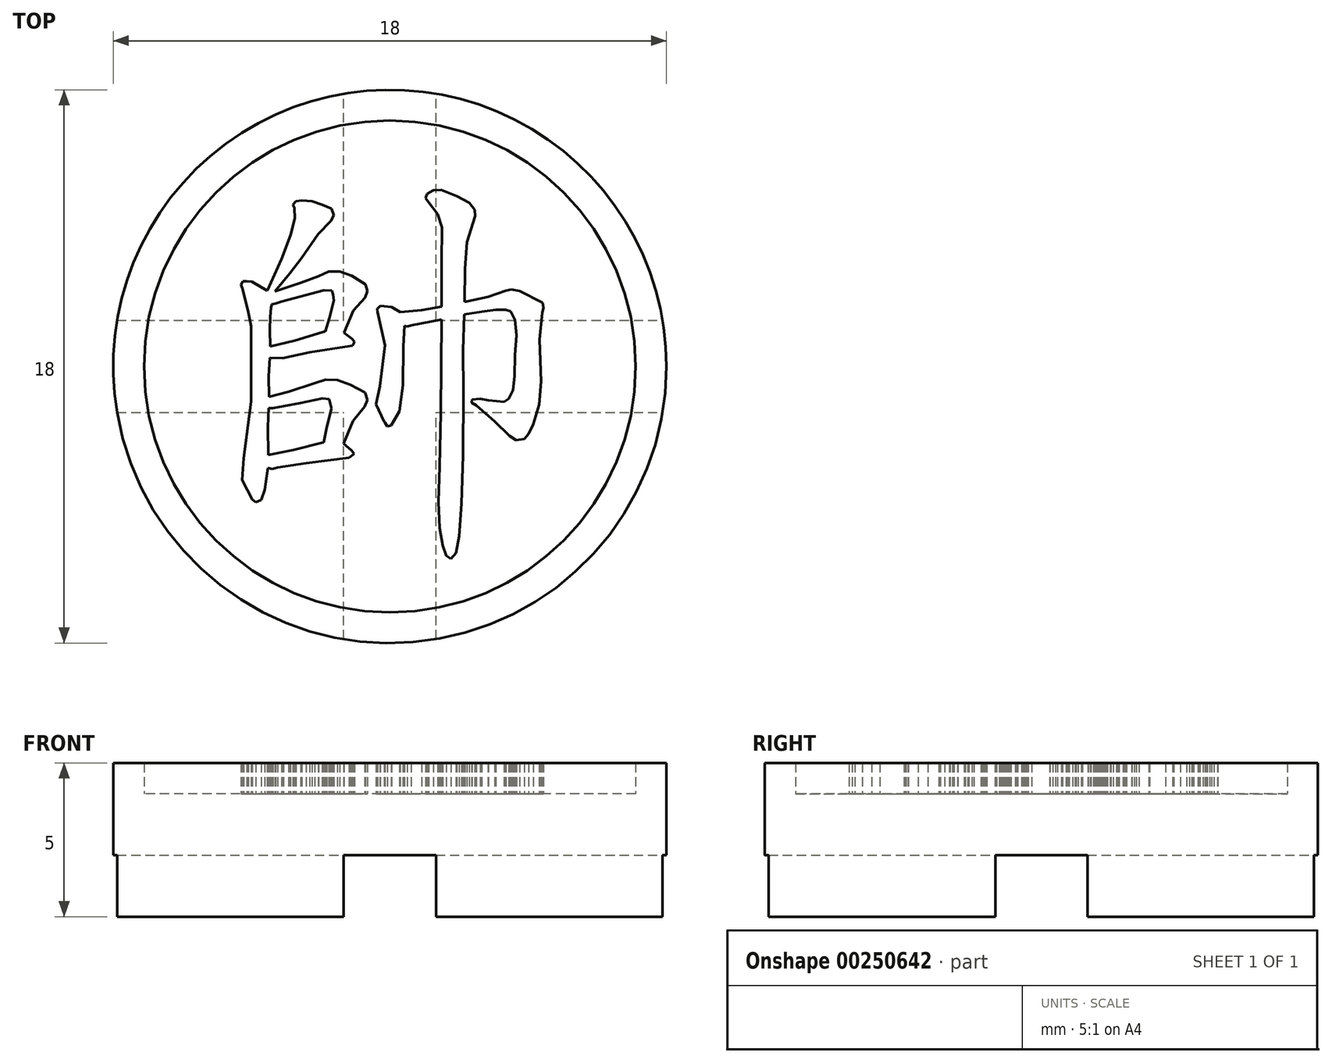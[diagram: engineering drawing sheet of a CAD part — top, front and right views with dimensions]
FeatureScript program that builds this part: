
annotation { "Feature Type Name" : "Feature", "Feature Type Description" : "" }
export const myFeature = defineFeature(function(context is Context, id is Id, definition is map)
    precondition{}
    {
        {
            var Q0;
            Q0=qCreatedBy(makeId("Top.planeOp"),FACE);
            var sketch = newSketch(context, id + "F0", { "sketchPlane" : qUnion([Q0])});
            skCircle(sketch, "E0", {"center": v(-31.33, 19.76) * mm, "radius": 9 * mm});
            skSolve(sketch);
        }
        {
            var Q0;
            Q0=qSketchRegion(id+"F0",true);
            extrude(context, id + "F1", {"entities" : qUnion([Q0]), "depth" : 4 * mm});
        }
        {
            var Q0;
            Q0=makeQuery(id+"F1.opExtrude","CAP_FACE",FACE,{"disambiguationData":[OSD([sQuery(id+"F0.wireOp",EDGE,"E0")])],"isStart":false});
            var sketch = newSketch(context, id + "F2", { "sketchPlane" : qUnion([Q0])});
            skCircle(sketch, "E1", {"center": v(-31.33, 19.76) * mm, "radius": 8 * mm});
            skCircle(sketch, "E2", {"center": v(-31.33, 19.76) * mm, "radius": 9 * mm});
            skSolve(sketch);
        }
        {
            var Q0;
            Q0=makeQuery(id+"F1.opExtrude","CAP_FACE",FACE,{"disambiguationData":[OSD([sQuery(id+"F0.wireOp",EDGE,"E0")])],"isStart":true});
            var sketch = newSketch(context, id + "F3", { "sketchPlane" : qUnion([Q0])});
            skLineSegment(sketch, "E3", {"start": v(-31.33, -19.76) * mm, "end": v(-22.33, -19.76) * mm, "construction": true});
            skLineSegment(sketch, "E4", {"start": v(-31.33, -19.76) * mm, "end": v(-31.33, -10.76) * mm, "construction": true});
            skLineSegment(sketch, "E5", {"start": v(-31.33, -19.76) * mm, "end": v(-40.33, -19.76) * mm, "construction": true});
            skLineSegment(sketch, "E6", {"start": v(-31.33, -19.76) * mm, "end": v(-31.33, -28.76) * mm, "construction": true});
            skLineSegment(sketch, "E7.bottom", {"start": v(-40.33, -28.76) * mm, "end": v(-22.33, -28.76) * mm});
            skLineSegment(sketch, "E7.top", {"start": v(-40.33, -10.76) * mm, "end": v(-22.33, -10.76) * mm});
            skLineSegment(sketch, "E7.left", {"start": v(-22.33, -10.76) * mm, "end": v(-22.33, -28.76) * mm});
            skLineSegment(sketch, "E7.right", {"start": v(-40.33, -10.76) * mm, "end": v(-40.33, -28.76) * mm});
            skPoint(sketch, "E8", {"position": v(-31.33, -28.76) * mm});
            skPoint(sketch, "E9", {"position": v(-40.33, -19.76) * mm});
            skPoint(sketch, "E10", {"position": v(-22.33, -19.76) * mm});
            skPoint(sketch, "E11", {"position": v(-31.33, -10.76) * mm});
            skLineSegment(sketch, "E12.bottom", {"start": v(-32.83, -10.76) * mm, "end": v(-29.83, -10.76) * mm});
            skLineSegment(sketch, "E12.top", {"start": v(-32.83, -28.76) * mm, "end": v(-29.83, -28.76) * mm});
            skLineSegment(sketch, "E12.left", {"start": v(-32.83, -10.76) * mm, "end": v(-32.83, -28.76) * mm});
            skLineSegment(sketch, "E12.right", {"start": v(-29.83, -10.76) * mm, "end": v(-29.83, -28.76) * mm});
            skLineSegment(sketch, "E13.bottom", {"start": v(-40.33, -18.26) * mm, "end": v(-22.33, -18.26) * mm});
            skLineSegment(sketch, "E13.top", {"start": v(-40.33, -21.26) * mm, "end": v(-22.33, -21.26) * mm});
            skLineSegment(sketch, "E13.left", {"start": v(-40.33, -18.26) * mm, "end": v(-40.33, -21.26) * mm});
            skLineSegment(sketch, "E13.right", {"start": v(-22.33, -18.26) * mm, "end": v(-22.33, -21.26) * mm});
            skSolve(sketch);
        }
        {
            var Q0;
            {var subQ1=sQuery(id+"F3.wireOp",EDGE,"E12.bottom");var subQ3=makeQuery(id+"F1.opExtrude","CAP_EDGE",EDGE,{"disambiguationData":[OSD([sQuery(id+"F0.wireOp",EDGE,"E0")])],"isStart":true});var subQ4=makeQuery(id+"F3.imprint","INTERSECT",VERTEX,{"derivedFrom":[subQ3,subQ1]});Q0=makeQuery(id+"F3.imprint","IMPRINT",FACE,{"disambiguationData":[TD([[makeQuery(id+"F3.imprint","IMPRINT",EDGE,{"disambiguationData":[TD([[subQ4,1.0]])],"derivedFrom":subQ3}),1.0]])]});}
            var Q1;
            {var subQ1=sQuery(id+"F3.wireOp",EDGE,"E12.bottom");var subQ3=makeQuery(id+"F1.opExtrude","CAP_EDGE",EDGE,{"disambiguationData":[OSD([sQuery(id+"F0.wireOp",EDGE,"E0")])],"isStart":true});var subQ4=makeQuery(id+"F3.imprint","INTERSECT",VERTEX,{"derivedFrom":[subQ3,subQ1]});Q1=makeQuery(id+"F3.imprint","IMPRINT",FACE,{"disambiguationData":[TD([[makeQuery(id+"F3.imprint","IMPRINT",EDGE,{"disambiguationData":[TD([[subQ4,-1.0]])],"derivedFrom":subQ3}),1.0]])]});}
            var Q2;
            {var subQ1=sQuery(id+"F3.wireOp",EDGE,"E12.top");var subQ3=makeQuery(id+"F1.opExtrude","CAP_EDGE",EDGE,{"disambiguationData":[OSD([sQuery(id+"F0.wireOp",EDGE,"E0")])],"isStart":true});var subQ4=makeQuery(id+"F3.imprint","INTERSECT",VERTEX,{"derivedFrom":[subQ3,subQ1]});Q2=makeQuery(id+"F3.imprint","IMPRINT",FACE,{"disambiguationData":[TD([[makeQuery(id+"F3.imprint","IMPRINT",EDGE,{"disambiguationData":[TD([[subQ4,-1.0]])],"derivedFrom":subQ3}),1.0]])]});}
            var Q3;
            {var subQ1=sQuery(id+"F3.wireOp",EDGE,"E12.top");var subQ3=makeQuery(id+"F1.opExtrude","CAP_EDGE",EDGE,{"disambiguationData":[OSD([sQuery(id+"F0.wireOp",EDGE,"E0")])],"isStart":true});var subQ4=makeQuery(id+"F3.imprint","INTERSECT",VERTEX,{"derivedFrom":[subQ3,subQ1]});Q3=makeQuery(id+"F3.imprint","IMPRINT",FACE,{"disambiguationData":[TD([[makeQuery(id+"F3.imprint","IMPRINT",EDGE,{"disambiguationData":[TD([[subQ4,1.0]])],"derivedFrom":subQ3}),1.0]])]});}
            var Q4;
            {var subQ0=sQuery(id+"F3.wireOp",EDGE,"E13.left");var subQ3=makeQuery(id+"F1.opExtrude","CAP_EDGE",EDGE,{"disambiguationData":[OSD([sQuery(id+"F0.wireOp",EDGE,"E0")])],"isStart":true});var subQ5=makeQuery(id+"F3.imprint","INTERSECT",VERTEX,{"derivedFrom":[subQ3,subQ0]});Q4=makeQuery(id+"F3.imprint","IMPRINT",FACE,{"disambiguationData":[TD([[makeQuery(id+"F3.imprint","IMPRINT",EDGE,{"disambiguationData":[TD([[subQ5,-1.0]])],"derivedFrom":subQ3}),1.0]])]});}
            var Q5;
            {var subQ0=sQuery(id+"F3.wireOp",EDGE,"E13.right");var subQ3=makeQuery(id+"F1.opExtrude","CAP_EDGE",EDGE,{"disambiguationData":[OSD([sQuery(id+"F0.wireOp",EDGE,"E0")])],"isStart":true});var subQ5=makeQuery(id+"F3.imprint","INTERSECT",VERTEX,{"derivedFrom":[subQ3,subQ0]});Q5=makeQuery(id+"F3.imprint","IMPRINT",FACE,{"disambiguationData":[TD([[makeQuery(id+"F3.imprint","IMPRINT",EDGE,{"disambiguationData":[TD([[subQ5,1.0]])],"derivedFrom":subQ3}),1.0]])]});}
            var Q6;
            {var subQ0=sQuery(id+"F3.wireOp",EDGE,"E13.left");var subQ3=makeQuery(id+"F1.opExtrude","CAP_EDGE",EDGE,{"disambiguationData":[OSD([sQuery(id+"F0.wireOp",EDGE,"E0")])],"isStart":true});var subQ5=makeQuery(id+"F3.imprint","INTERSECT",VERTEX,{"derivedFrom":[subQ3,subQ0]});Q6=makeQuery(id+"F3.imprint","IMPRINT",FACE,{"disambiguationData":[TD([[makeQuery(id+"F3.imprint","IMPRINT",EDGE,{"disambiguationData":[TD([[subQ5,1.0]])],"derivedFrom":subQ3}),1.0]])]});}
            var Q7;
            {var subQ0=sQuery(id+"F3.wireOp",EDGE,"E13.right");var subQ3=makeQuery(id+"F1.opExtrude","CAP_EDGE",EDGE,{"disambiguationData":[OSD([sQuery(id+"F0.wireOp",EDGE,"E0")])],"isStart":true});var subQ5=makeQuery(id+"F3.imprint","INTERSECT",VERTEX,{"derivedFrom":[subQ3,subQ0]});Q7=makeQuery(id+"F3.imprint","IMPRINT",FACE,{"disambiguationData":[TD([[makeQuery(id+"F3.imprint","IMPRINT",EDGE,{"disambiguationData":[TD([[subQ5,-1.0]])],"derivedFrom":subQ3}),1.0]])]});}
            var Q8;
            {var subQ3=makeQuery(id+"F1.opExtrude","CAP_EDGE",EDGE,{"disambiguationData":[OSD([sQuery(id+"F0.wireOp",EDGE,"E0")])],"isStart":true});var subQ5=sQuery(id+"F3.wireOp",EDGE,"E12.left");var subQ8=makeQuery(id+"F3.imprint","INTERSECT",VERTEX,{"disambiguationData":[OD(1.0)],"derivedFrom":[subQ3,subQ5]});Q8=makeQuery(id+"F3.imprint","IMPRINT",FACE,{"disambiguationData":[TD([[makeQuery(id+"F3.imprint","IMPRINT",EDGE,{"disambiguationData":[TD([[subQ8,-1.0]])],"derivedFrom":subQ3}),1.0]])]});}
            var Q9;
            {var subQ3=makeQuery(id+"F1.opExtrude","CAP_EDGE",EDGE,{"disambiguationData":[OSD([sQuery(id+"F0.wireOp",EDGE,"E0")])],"isStart":true});var subQ5=sQuery(id+"F3.wireOp",EDGE,"E12.right");var subQ8=makeQuery(id+"F3.imprint","INTERSECT",VERTEX,{"disambiguationData":[OD(1.0)],"derivedFrom":[subQ3,subQ5]});Q9=makeQuery(id+"F3.imprint","IMPRINT",FACE,{"disambiguationData":[TD([[makeQuery(id+"F3.imprint","IMPRINT",EDGE,{"disambiguationData":[TD([[subQ8,1.0]])],"derivedFrom":subQ3}),1.0]])]});}
            var Q10;
            {var subQ3=makeQuery(id+"F1.opExtrude","CAP_EDGE",EDGE,{"disambiguationData":[OSD([sQuery(id+"F0.wireOp",EDGE,"E0")])],"isStart":true});var subQ5=sQuery(id+"F3.wireOp",EDGE,"E12.left");var subQ8=makeQuery(id+"F3.imprint","INTERSECT",VERTEX,{"disambiguationData":[OD(0.0)],"derivedFrom":[subQ3,subQ5]});Q10=makeQuery(id+"F3.imprint","IMPRINT",FACE,{"disambiguationData":[TD([[makeQuery(id+"F3.imprint","IMPRINT",EDGE,{"disambiguationData":[TD([[subQ8,1.0]])],"derivedFrom":subQ3}),1.0]])]});}
            var Q11;
            {var subQ3=makeQuery(id+"F1.opExtrude","CAP_EDGE",EDGE,{"disambiguationData":[OSD([sQuery(id+"F0.wireOp",EDGE,"E0")])],"isStart":true});var subQ5=sQuery(id+"F3.wireOp",EDGE,"E12.right");var subQ8=makeQuery(id+"F3.imprint","INTERSECT",VERTEX,{"disambiguationData":[OD(0.0)],"derivedFrom":[subQ3,subQ5]});Q11=makeQuery(id+"F3.imprint","IMPRINT",FACE,{"disambiguationData":[TD([[makeQuery(id+"F3.imprint","IMPRINT",EDGE,{"disambiguationData":[TD([[subQ8,-1.0]])],"derivedFrom":subQ3}),1.0]])]});}
            var Q12;
            {var subQ2=sQuery(id+"F3.wireOp",EDGE,"E12.left");var subQ4=sQuery(id+"F3.wireOp",EDGE,"E13.bottom");var subQ8=makeQuery(id+"F3.imprint","INTERSECT",VERTEX,{"derivedFrom":[subQ2,subQ4]});Q12=makeQuery(id+"F3.imprint","IMPRINT",FACE,{"disambiguationData":[TD([[makeQuery(id+"F3.imprint","IMPRINT",EDGE,{"disambiguationData":[TD([[subQ8,1.0]])],"derivedFrom":subQ2}),1.0]])]});}
            var Q13;
            {var subQ1=sQuery(id+"F3.wireOp",EDGE,"E12.left");var subQ5=sQuery(id+"F3.wireOp",EDGE,"E13.bottom");var subQ6=makeQuery(id+"F3.imprint","INTERSECT",VERTEX,{"derivedFrom":[subQ1,subQ5]});Q13=makeQuery(id+"F3.imprint","IMPRINT",FACE,{"disambiguationData":[TD([[makeQuery(id+"F3.imprint","IMPRINT",EDGE,{"disambiguationData":[TD([[subQ6,-1.0]])],"derivedFrom":subQ1}),-1.0]])]});}
            var Q14;
            {var subQ0=sQuery(id+"F3.wireOp",EDGE,"E13.top");var subQ1=sQuery(id+"F3.wireOp",EDGE,"E12.left");var subQ2=makeQuery(id+"F3.imprint","INTERSECT",VERTEX,{"derivedFrom":[subQ1,subQ0]});Q14=makeQuery(id+"F3.imprint","IMPRINT",FACE,{"disambiguationData":[TD([[makeQuery(id+"F3.imprint","IMPRINT",EDGE,{"disambiguationData":[TD([[subQ2,-1.0]])],"derivedFrom":subQ1}),1.0]])]});}
            var Q15;
            {var subQ2=sQuery(id+"F3.wireOp",EDGE,"E13.bottom");var subQ5=sQuery(id+"F3.wireOp",EDGE,"E12.right");var subQ8=makeQuery(id+"F3.imprint","INTERSECT",VERTEX,{"derivedFrom":[subQ5,subQ2]});Q15=makeQuery(id+"F3.imprint","IMPRINT",FACE,{"disambiguationData":[TD([[makeQuery(id+"F3.imprint","IMPRINT",EDGE,{"disambiguationData":[TD([[subQ8,-1.0]])],"derivedFrom":subQ5}),1.0]])]});}
            var Q16;
            {var subQ0=sQuery(id+"F3.wireOp",EDGE,"E13.bottom");var subQ1=sQuery(id+"F3.wireOp",EDGE,"E12.left");var subQ2=makeQuery(id+"F3.imprint","INTERSECT",VERTEX,{"derivedFrom":[subQ1,subQ0]});Q16=makeQuery(id+"F3.imprint","IMPRINT",FACE,{"disambiguationData":[TD([[makeQuery(id+"F3.imprint","IMPRINT",EDGE,{"disambiguationData":[TD([[subQ2,-1.0]])],"derivedFrom":subQ1}),1.0]])]});}
            extrude(context, id + "F4", {"entities" : qUnion([Q0, Q1, Q2, Q3, Q4, Q5, Q6, Q7, Q8, Q9, Q10, Q11, Q12, Q13, Q14, Q15, Q16]), "operationType" : NewBodyOperationType.REMOVE, "oppositeDirection" : true, "depth" : 2 * mm});
        }
        {
            var Q0;
            Q0=qSketchRegion(id+"F2",true);
            var Q1;
            Q1=makeQuery(id+"F2.imprint","IMPRINT",FACE,{"disambiguationData":[TD([[makeQuery(id+"F2.imprint","IMPRINT",EDGE,{"derivedFrom":sQuery(id+"F2.wireOp",EDGE,"hKqnuJLd-dfdz-vJIs-yDKo-c4hLNRw30SuP")}),-1.0]])]});
            extrude(context, id + "F5", {"entities" : qUnion([Q0, Q1]), "operationType" : NewBodyOperationType.ADD, "depth" : 1 * mm});
        }
        {
            var Q0;
            Q0=makeQuery(id+"F1.opExtrude","CAP_FACE",FACE,{"disambiguationData":[OSD([sQuery(id+"F0.wireOp",EDGE,"E0")])],"isStart":false});
            var sketch = newSketch(context, id + "F6", { "sketchPlane" : qUnion([Q0])});
            skLineSegment(sketch, "E14", {"start": v(-35.3, 16.46) * mm, "end": v(-35.16, 16.42) * mm});
            skLineSegment(sketch, "E15", {"start": v(-35.16, 16.42) * mm, "end": v(-34.98, 16.47) * mm});
            skLineSegment(sketch, "E16", {"start": v(-34.98, 16.47) * mm, "end": v(-34.06, 16.61) * mm});
            skLineSegment(sketch, "E17", {"start": v(-34.06, 16.61) * mm, "end": v(-32.65, 16.79) * mm});
            skLineSegment(sketch, "E18", {"start": v(-32.65, 16.79) * mm, "end": v(-32.5, 16.92) * mm});
            skLineSegment(sketch, "E19", {"start": v(-32.5, 16.92) * mm, "end": v(-32.59, 17.04) * mm});
            skLineSegment(sketch, "E20", {"start": v(-32.59, 17.04) * mm, "end": v(-32.84, 17.25) * mm});
            skLineSegment(sketch, "E21", {"start": v(-32.84, 17.25) * mm, "end": v(-32.52, 17.98) * mm});
            skLineSegment(sketch, "E22", {"start": v(-32.52, 17.98) * mm, "end": v(-32.15, 18.46) * mm});
            skLineSegment(sketch, "E23", {"start": v(-32.15, 18.46) * mm, "end": v(-32.06, 18.67) * mm});
            skLineSegment(sketch, "E24", {"start": v(-32.06, 18.67) * mm, "end": v(-32.14, 18.9) * mm});
            skLineSegment(sketch, "E25", {"start": v(-32.14, 18.9) * mm, "end": v(-32.62, 19.16) * mm});
            skLineSegment(sketch, "E26", {"start": v(-32.62, 19.16) * mm, "end": v(-33.04, 19.31) * mm});
            skLineSegment(sketch, "E27", {"start": v(-33.04, 19.31) * mm, "end": v(-33.42, 19.33) * mm});
            skLineSegment(sketch, "E28", {"start": v(-33.42, 19.33) * mm, "end": v(-33.77, 19.21) * mm});
            skLineSegment(sketch, "E29", {"start": v(-33.77, 19.21) * mm, "end": v(-34.63, 18.93) * mm});
            skLineSegment(sketch, "E30", {"start": v(-34.63, 18.93) * mm, "end": v(-35.26, 18.77) * mm});
            skLineSegment(sketch, "E31", {"start": v(-35.26, 18.77) * mm, "end": v(-35.27, 19.44) * mm});
            skLineSegment(sketch, "E32", {"start": v(-35.27, 19.44) * mm, "end": v(-35.24, 20.04) * mm});
            skLineSegment(sketch, "E33", {"start": v(-35.24, 20.04) * mm, "end": v(-34.81, 20.03) * mm});
            skLineSegment(sketch, "E34", {"start": v(-34.81, 20.03) * mm, "end": v(-33.94, 20.22) * mm});
            skLineSegment(sketch, "E35", {"start": v(-33.94, 20.22) * mm, "end": v(-32.63, 20.42) * mm});
            skLineSegment(sketch, "E36", {"start": v(-32.63, 20.42) * mm, "end": v(-32.54, 20.44) * mm});
            skLineSegment(sketch, "E37", {"start": v(-32.54, 20.44) * mm, "end": v(-32.48, 20.57) * mm});
            skLineSegment(sketch, "E38", {"start": v(-32.48, 20.57) * mm, "end": v(-32.57, 20.67) * mm});
            skLineSegment(sketch, "E39", {"start": v(-32.57, 20.67) * mm, "end": v(-32.82, 20.86) * mm});
            skLineSegment(sketch, "E40", {"start": v(-32.82, 20.86) * mm, "end": v(-32.51, 21.58) * mm});
            skLineSegment(sketch, "E41", {"start": v(-32.51, 21.58) * mm, "end": v(-32.14, 22) * mm});
            skLineSegment(sketch, "E42", {"start": v(-32.14, 22) * mm, "end": v(-32.06, 22.2) * mm});
            skLineSegment(sketch, "E43", {"start": v(-32.06, 22.2) * mm, "end": v(-32.12, 22.42) * mm});
            skLineSegment(sketch, "E44", {"start": v(-32.12, 22.42) * mm, "end": v(-32.57, 22.7) * mm});
            skLineSegment(sketch, "E45", {"start": v(-32.57, 22.7) * mm, "end": v(-32.97, 22.85) * mm});
            skLineSegment(sketch, "E46", {"start": v(-32.97, 22.85) * mm, "end": v(-33.32, 22.84) * mm});
            skLineSegment(sketch, "E47", {"start": v(-33.32, 22.84) * mm, "end": v(-33.65, 22.7) * mm});
            skLineSegment(sketch, "E48", {"start": v(-33.65, 22.7) * mm, "end": v(-34.23, 22.48) * mm});
            skLineSegment(sketch, "E49", {"start": v(-34.23, 22.48) * mm, "end": v(-35.08, 22.2) * mm});
            skLineSegment(sketch, "E50", {"start": v(-35.08, 22.2) * mm, "end": v(-34.6, 22.79) * mm});
            skLineSegment(sketch, "E51", {"start": v(-34.6, 22.79) * mm, "end": v(-34.2, 23.28) * mm});
            skLineSegment(sketch, "E52", {"start": v(-34.2, 23.28) * mm, "end": v(-33.66, 24.06) * mm});
            skLineSegment(sketch, "E53", {"start": v(-33.66, 24.06) * mm, "end": v(-33.26, 24.5) * mm});
            skLineSegment(sketch, "E54", {"start": v(-33.26, 24.5) * mm, "end": v(-33.15, 24.68) * mm});
            skLineSegment(sketch, "E55", {"start": v(-33.15, 24.68) * mm, "end": v(-33.23, 24.89) * mm});
            skLineSegment(sketch, "E56", {"start": v(-33.23, 24.89) * mm, "end": v(-33.54, 25.02) * mm});
            skLineSegment(sketch, "E57", {"start": v(-33.54, 25.02) * mm, "end": v(-33.87, 25.14) * mm});
            skLineSegment(sketch, "E58", {"start": v(-33.87, 25.14) * mm, "end": v(-34.2, 25.16) * mm});
            skLineSegment(sketch, "E59", {"start": v(-34.2, 25.16) * mm, "end": v(-34.38, 25.14) * mm});
            skLineSegment(sketch, "E60", {"start": v(-34.38, 25.14) * mm, "end": v(-34.49, 25.03) * mm});
            skLineSegment(sketch, "E61", {"start": v(-34.49, 25.03) * mm, "end": v(-34.43, 24.91) * mm});
            skLineSegment(sketch, "E62", {"start": v(-34.43, 24.91) * mm, "end": v(-34.42, 24.58) * mm});
            skLineSegment(sketch, "E63", {"start": v(-34.42, 24.58) * mm, "end": v(-34.56, 24.03) * mm});
            skLineSegment(sketch, "E64", {"start": v(-34.56, 24.03) * mm, "end": v(-34.86, 23.25) * mm});
            skLineSegment(sketch, "E65", {"start": v(-34.86, 23.25) * mm, "end": v(-35.31, 22.24) * mm});
            skLineSegment(sketch, "E66", {"start": v(-35.31, 22.24) * mm, "end": v(-35.33, 22.23) * mm});
            skLineSegment(sketch, "E67", {"start": v(-35.33, 22.23) * mm, "end": v(-35.81, 22.52) * mm});
            skLineSegment(sketch, "E68", {"start": v(-35.81, 22.52) * mm, "end": v(-35.98, 22.53) * mm});
            skLineSegment(sketch, "E69", {"start": v(-35.98, 22.53) * mm, "end": v(-36.1, 22.53) * mm});
            skLineSegment(sketch, "E70", {"start": v(-36.1, 22.53) * mm, "end": v(-36.17, 22.42) * mm});
            skLineSegment(sketch, "E71", {"start": v(-36.17, 22.42) * mm, "end": v(-36.12, 22.3) * mm});
            skLineSegment(sketch, "E72", {"start": v(-36.12, 22.3) * mm, "end": v(-35.94, 21.51) * mm});
            skLineSegment(sketch, "E73", {"start": v(-35.94, 21.51) * mm, "end": v(-35.84, 21.07) * mm});
            skLineSegment(sketch, "E74", {"start": v(-35.84, 21.07) * mm, "end": v(-35.85, 18.63) * mm});
            skLineSegment(sketch, "E75", {"start": v(-35.85, 18.63) * mm, "end": v(-36.1, 16.77) * mm});
            skLineSegment(sketch, "E76", {"start": v(-36.1, 16.77) * mm, "end": v(-36.14, 16.07) * mm});
            skLineSegment(sketch, "E77", {"start": v(-36.14, 16.07) * mm, "end": v(-35.8, 15.43) * mm});
            skLineSegment(sketch, "E78", {"start": v(-35.8, 15.43) * mm, "end": v(-35.7, 15.34) * mm});
            skLineSegment(sketch, "E79", {"start": v(-35.7, 15.34) * mm, "end": v(-35.51, 15.41) * mm});
            skLineSegment(sketch, "E80", {"start": v(-35.51, 15.41) * mm, "end": v(-35.4, 15.75) * mm});
            skLineSegment(sketch, "E81", {"start": v(-35.4, 15.75) * mm, "end": v(-35.3, 16.46) * mm});
            skLineSegment(sketch, "E82", {"start": v(-33.5, 17.29) * mm, "end": v(-34.46, 17.04) * mm});
            skLineSegment(sketch, "E83", {"start": v(-34.46, 17.04) * mm, "end": v(-35.29, 16.88) * mm});
            skLineSegment(sketch, "E84", {"start": v(-35.29, 16.88) * mm, "end": v(-35.3, 17.8) * mm});
            skLineSegment(sketch, "E85", {"start": v(-35.3, 17.8) * mm, "end": v(-35.28, 18.4) * mm});
            skLineSegment(sketch, "E86", {"start": v(-35.28, 18.4) * mm, "end": v(-35.13, 18.4) * mm});
            skLineSegment(sketch, "E87", {"start": v(-35.13, 18.4) * mm, "end": v(-34.79, 18.46) * mm});
            skLineSegment(sketch, "E88", {"start": v(-34.79, 18.46) * mm, "end": v(-34.25, 18.57) * mm});
            skLineSegment(sketch, "E89", {"start": v(-34.25, 18.57) * mm, "end": v(-33.52, 18.72) * mm});
            skLineSegment(sketch, "E90", {"start": v(-33.52, 18.72) * mm, "end": v(-33.31, 18.7) * mm});
            skLineSegment(sketch, "E91", {"start": v(-33.31, 18.7) * mm, "end": v(-33.23, 18.4) * mm});
            skLineSegment(sketch, "E92", {"start": v(-33.23, 18.4) * mm, "end": v(-33.38, 17.8) * mm});
            skLineSegment(sketch, "E93", {"start": v(-33.38, 17.8) * mm, "end": v(-33.48, 17.29) * mm});
            skLineSegment(sketch, "E94", {"start": v(-33.48, 17.29) * mm, "end": v(-33.5, 17.29) * mm});
            skLineSegment(sketch, "E95", {"start": v(-33.5, 20.88) * mm, "end": v(-34.43, 20.6) * mm});
            skLineSegment(sketch, "E96", {"start": v(-34.43, 20.6) * mm, "end": v(-35.22, 20.41) * mm});
            skLineSegment(sketch, "E97", {"start": v(-35.22, 20.41) * mm, "end": v(-35.24, 20.96) * mm});
            skLineSegment(sketch, "E98", {"start": v(-35.24, 20.96) * mm, "end": v(-35.23, 21.38) * mm});
            skLineSegment(sketch, "E99", {"start": v(-35.23, 21.38) * mm, "end": v(-35.2, 21.66) * mm});
            skLineSegment(sketch, "E100", {"start": v(-35.2, 21.66) * mm, "end": v(-35.17, 21.78) * mm});
            skLineSegment(sketch, "E101", {"start": v(-35.17, 21.78) * mm, "end": v(-35.05, 21.8) * mm});
            skLineSegment(sketch, "E102", {"start": v(-35.05, 21.8) * mm, "end": v(-34.85, 21.87) * mm});
            skLineSegment(sketch, "E103", {"start": v(-34.85, 21.87) * mm, "end": v(-33.47, 22.24) * mm});
            skLineSegment(sketch, "E104", {"start": v(-33.47, 22.24) * mm, "end": v(-33.22, 22.23) * mm});
            skLineSegment(sketch, "E105", {"start": v(-33.22, 22.23) * mm, "end": v(-33.18, 22.1) * mm});
            skLineSegment(sketch, "E106", {"start": v(-33.18, 22.1) * mm, "end": v(-33.15, 21.91) * mm});
            skLineSegment(sketch, "E107", {"start": v(-33.15, 21.91) * mm, "end": v(-33.3, 21.35) * mm});
            skLineSegment(sketch, "E108", {"start": v(-33.3, 21.35) * mm, "end": v(-33.43, 20.9) * mm});
            skLineSegment(sketch, "E109", {"start": v(-33.43, 20.9) * mm, "end": v(-33.5, 20.9) * mm});
            skLineSegment(sketch, "E110", {"start": v(-33.5, 20.9) * mm, "end": v(-33.5, 20.88) * mm});
            skLineSegment(sketch, "E111", {"start": v(-29.65, 21.3) * mm, "end": v(-29.67, 18.25) * mm});
            skLineSegment(sketch, "E112", {"start": v(-29.67, 18.25) * mm, "end": v(-29.72, 16.5) * mm});
            skLineSegment(sketch, "E113", {"start": v(-29.72, 16.5) * mm, "end": v(-29.75, 15.36) * mm});
            skLineSegment(sketch, "E114", {"start": v(-29.75, 15.36) * mm, "end": v(-29.7, 14.5) * mm});
            skLineSegment(sketch, "E115", {"start": v(-29.7, 14.5) * mm, "end": v(-29.61, 13.93) * mm});
            skLineSegment(sketch, "E116", {"start": v(-29.61, 13.93) * mm, "end": v(-29.5, 13.6) * mm});
            skLineSegment(sketch, "E117", {"start": v(-29.5, 13.6) * mm, "end": v(-29.34, 13.5) * mm});
            skLineSegment(sketch, "E118", {"start": v(-29.34, 13.5) * mm, "end": v(-29.17, 13.69) * mm});
            skLineSegment(sketch, "E119", {"start": v(-29.17, 13.69) * mm, "end": v(-29.08, 14.24) * mm});
            skLineSegment(sketch, "E120", {"start": v(-29.08, 14.24) * mm, "end": v(-29, 15.3) * mm});
            skLineSegment(sketch, "E121", {"start": v(-29, 15.3) * mm, "end": v(-28.95, 16.86) * mm});
            skLineSegment(sketch, "E122", {"start": v(-28.95, 16.86) * mm, "end": v(-28.94, 18.93) * mm});
            skLineSegment(sketch, "E123", {"start": v(-28.94, 18.93) * mm, "end": v(-28.95, 20.28) * mm});
            skLineSegment(sketch, "E124", {"start": v(-28.95, 20.28) * mm, "end": v(-28.91, 21.45) * mm});
            skLineSegment(sketch, "E125", {"start": v(-28.91, 21.45) * mm, "end": v(-28.33, 21.54) * mm});
            skLineSegment(sketch, "E126", {"start": v(-28.33, 21.54) * mm, "end": v(-27.88, 21.6) * mm});
            skLineSegment(sketch, "E127", {"start": v(-27.88, 21.6) * mm, "end": v(-27.56, 21.6) * mm});
            skLineSegment(sketch, "E128", {"start": v(-27.56, 21.6) * mm, "end": v(-27.4, 21.56) * mm});
            skLineSegment(sketch, "E129", {"start": v(-27.4, 21.56) * mm, "end": v(-27.26, 21.27) * mm});
            skLineSegment(sketch, "E130", {"start": v(-27.26, 21.27) * mm, "end": v(-27.21, 20.78) * mm});
            skLineSegment(sketch, "E131", {"start": v(-27.21, 20.78) * mm, "end": v(-27.26, 20.13) * mm});
            skLineSegment(sketch, "E132", {"start": v(-27.26, 20.13) * mm, "end": v(-27.28, 19.45) * mm});
            skLineSegment(sketch, "E133", {"start": v(-27.28, 19.45) * mm, "end": v(-27.33, 18.99) * mm});
            skLineSegment(sketch, "E134", {"start": v(-27.33, 18.99) * mm, "end": v(-27.46, 18.71) * mm});
            skLineSegment(sketch, "E135", {"start": v(-27.46, 18.71) * mm, "end": v(-27.6, 18.6) * mm});
            skLineSegment(sketch, "E136", {"start": v(-27.6, 18.6) * mm, "end": v(-27.86, 18.63) * mm});
            skLineSegment(sketch, "E137", {"start": v(-27.86, 18.63) * mm, "end": v(-28.13, 18.65) * mm});
            skLineSegment(sketch, "E138", {"start": v(-28.13, 18.65) * mm, "end": v(-28.39, 18.71) * mm});
            skLineSegment(sketch, "E139", {"start": v(-28.39, 18.71) * mm, "end": v(-28.66, 18.68) * mm});
            skLineSegment(sketch, "E140", {"start": v(-28.66, 18.68) * mm, "end": v(-28.67, 18.58) * mm});
            skLineSegment(sketch, "E141", {"start": v(-28.67, 18.58) * mm, "end": v(-28.52, 18.49) * mm});
            skLineSegment(sketch, "E142", {"start": v(-28.52, 18.49) * mm, "end": v(-27.92, 17.97) * mm});
            skLineSegment(sketch, "E143", {"start": v(-27.92, 17.97) * mm, "end": v(-27.44, 17.5) * mm});
            skLineSegment(sketch, "E144", {"start": v(-27.44, 17.5) * mm, "end": v(-27.22, 17.36) * mm});
            skLineSegment(sketch, "E145", {"start": v(-27.22, 17.36) * mm, "end": v(-26.96, 17.4) * mm});
            skLineSegment(sketch, "E146", {"start": v(-26.96, 17.4) * mm, "end": v(-26.82, 17.56) * mm});
            skLineSegment(sketch, "E147", {"start": v(-26.82, 17.56) * mm, "end": v(-26.66, 17.88) * mm});
            skLineSegment(sketch, "E148", {"start": v(-26.66, 17.88) * mm, "end": v(-26.48, 18.52) * mm});
            skLineSegment(sketch, "E149", {"start": v(-26.48, 18.52) * mm, "end": v(-26.4, 19.26) * mm});
            skLineSegment(sketch, "E150", {"start": v(-26.4, 19.26) * mm, "end": v(-26.46, 20.64) * mm});
            skLineSegment(sketch, "E151", {"start": v(-26.46, 20.64) * mm, "end": v(-26.37, 21.5) * mm});
            skLineSegment(sketch, "E152", {"start": v(-26.37, 21.5) * mm, "end": v(-26.33, 21.67) * mm});
            skLineSegment(sketch, "E153", {"start": v(-26.33, 21.67) * mm, "end": v(-26.36, 21.83) * mm});
            skLineSegment(sketch, "E154", {"start": v(-26.36, 21.83) * mm, "end": v(-27.1, 22.21) * mm});
            skLineSegment(sketch, "E155", {"start": v(-27.1, 22.21) * mm, "end": v(-27.37, 22.26) * mm});
            skLineSegment(sketch, "E156", {"start": v(-27.37, 22.26) * mm, "end": v(-27.56, 22.23) * mm});
            skLineSegment(sketch, "E157", {"start": v(-27.56, 22.23) * mm, "end": v(-28.14, 22.02) * mm});
            skLineSegment(sketch, "E158", {"start": v(-28.14, 22.02) * mm, "end": v(-28.9, 21.86) * mm});
            skLineSegment(sketch, "E159", {"start": v(-28.9, 21.86) * mm, "end": v(-28.9, 22.94) * mm});
            skLineSegment(sketch, "E160", {"start": v(-28.9, 22.94) * mm, "end": v(-28.82, 23.8) * mm});
            skLineSegment(sketch, "E161", {"start": v(-28.82, 23.8) * mm, "end": v(-28.56, 24.65) * mm});
            skLineSegment(sketch, "E162", {"start": v(-28.56, 24.65) * mm, "end": v(-28.56, 24.85) * mm});
            skLineSegment(sketch, "E163", {"start": v(-28.56, 24.85) * mm, "end": v(-28.74, 25.08) * mm});
            skLineSegment(sketch, "E164", {"start": v(-28.74, 25.08) * mm, "end": v(-29.15, 25.3) * mm});
            skLineSegment(sketch, "E165", {"start": v(-29.15, 25.3) * mm, "end": v(-29.66, 25.5) * mm});
            skLineSegment(sketch, "E166", {"start": v(-29.66, 25.5) * mm, "end": v(-29.92, 25.5) * mm});
            skLineSegment(sketch, "E167", {"start": v(-29.92, 25.5) * mm, "end": v(-30.11, 25.37) * mm});
            skLineSegment(sketch, "E168", {"start": v(-30.11, 25.37) * mm, "end": v(-30.17, 25.24) * mm});
            skLineSegment(sketch, "E169", {"start": v(-30.17, 25.24) * mm, "end": v(-30.07, 25.1) * mm});
            skLineSegment(sketch, "E170", {"start": v(-30.07, 25.1) * mm, "end": v(-29.77, 24.72) * mm});
            skLineSegment(sketch, "E171", {"start": v(-29.77, 24.72) * mm, "end": v(-29.64, 24.28) * mm});
            skLineSegment(sketch, "E172", {"start": v(-29.64, 24.28) * mm, "end": v(-29.65, 23.14) * mm});
            skLineSegment(sketch, "E173", {"start": v(-29.65, 23.14) * mm, "end": v(-29.65, 21.7) * mm});
            skLineSegment(sketch, "E174", {"start": v(-29.65, 21.7) * mm, "end": v(-30.3, 21.59) * mm});
            skLineSegment(sketch, "E175", {"start": v(-30.3, 21.59) * mm, "end": v(-31, 21.53) * mm});
            skLineSegment(sketch, "E176", {"start": v(-31, 21.53) * mm, "end": v(-31.27, 21.7) * mm});
            skLineSegment(sketch, "E177", {"start": v(-31.27, 21.7) * mm, "end": v(-31.64, 21.73) * mm});
            skLineSegment(sketch, "E178", {"start": v(-31.64, 21.73) * mm, "end": v(-31.75, 21.63) * mm});
            skLineSegment(sketch, "E179", {"start": v(-31.75, 21.63) * mm, "end": v(-31.73, 21.53) * mm});
            skLineSegment(sketch, "E180", {"start": v(-31.73, 21.53) * mm, "end": v(-31.5, 20.45) * mm});
            skLineSegment(sketch, "E181", {"start": v(-31.5, 20.45) * mm, "end": v(-31.65, 19.12) * mm});
            skLineSegment(sketch, "E182", {"start": v(-31.65, 19.12) * mm, "end": v(-31.78, 18.53) * mm});
            skLineSegment(sketch, "E183", {"start": v(-31.78, 18.53) * mm, "end": v(-31.52, 17.96) * mm});
            skLineSegment(sketch, "E184", {"start": v(-31.52, 17.96) * mm, "end": v(-31.5, 17.93) * mm});
            skLineSegment(sketch, "E185", {"start": v(-31.5, 17.93) * mm, "end": v(-31.41, 17.8) * mm});
            skLineSegment(sketch, "E186", {"start": v(-31.41, 17.8) * mm, "end": v(-31.28, 17.84) * mm});
            skLineSegment(sketch, "E187", {"start": v(-31.28, 17.84) * mm, "end": v(-31.02, 18.3) * mm});
            skLineSegment(sketch, "E188", {"start": v(-31.02, 18.3) * mm, "end": v(-30.9, 19.16) * mm});
            skLineSegment(sketch, "E189", {"start": v(-30.9, 19.16) * mm, "end": v(-30.9, 20.4) * mm});
            skLineSegment(sketch, "E190", {"start": v(-30.9, 20.4) * mm, "end": v(-30.85, 21.08) * mm});
            skLineSegment(sketch, "E191", {"start": v(-30.85, 21.08) * mm, "end": v(-30.77, 21.06) * mm});
            skLineSegment(sketch, "E192", {"start": v(-30.77, 21.06) * mm, "end": v(-30.64, 21.1) * mm});
            skLineSegment(sketch, "E193", {"start": v(-30.64, 21.1) * mm, "end": v(-29.65, 21.3) * mm});
            skSolve(sketch);
        }
        {
            var Q0;
            Q0 = qSketchRegion(id + "F6", true);
            extrude(context, id + "F7", {"entities" : qUnion([Q0]), "operationType" : NewBodyOperationType.ADD, "depth" : 1 * mm, "offsetDistance" : 25 * mm});
        }
    });
